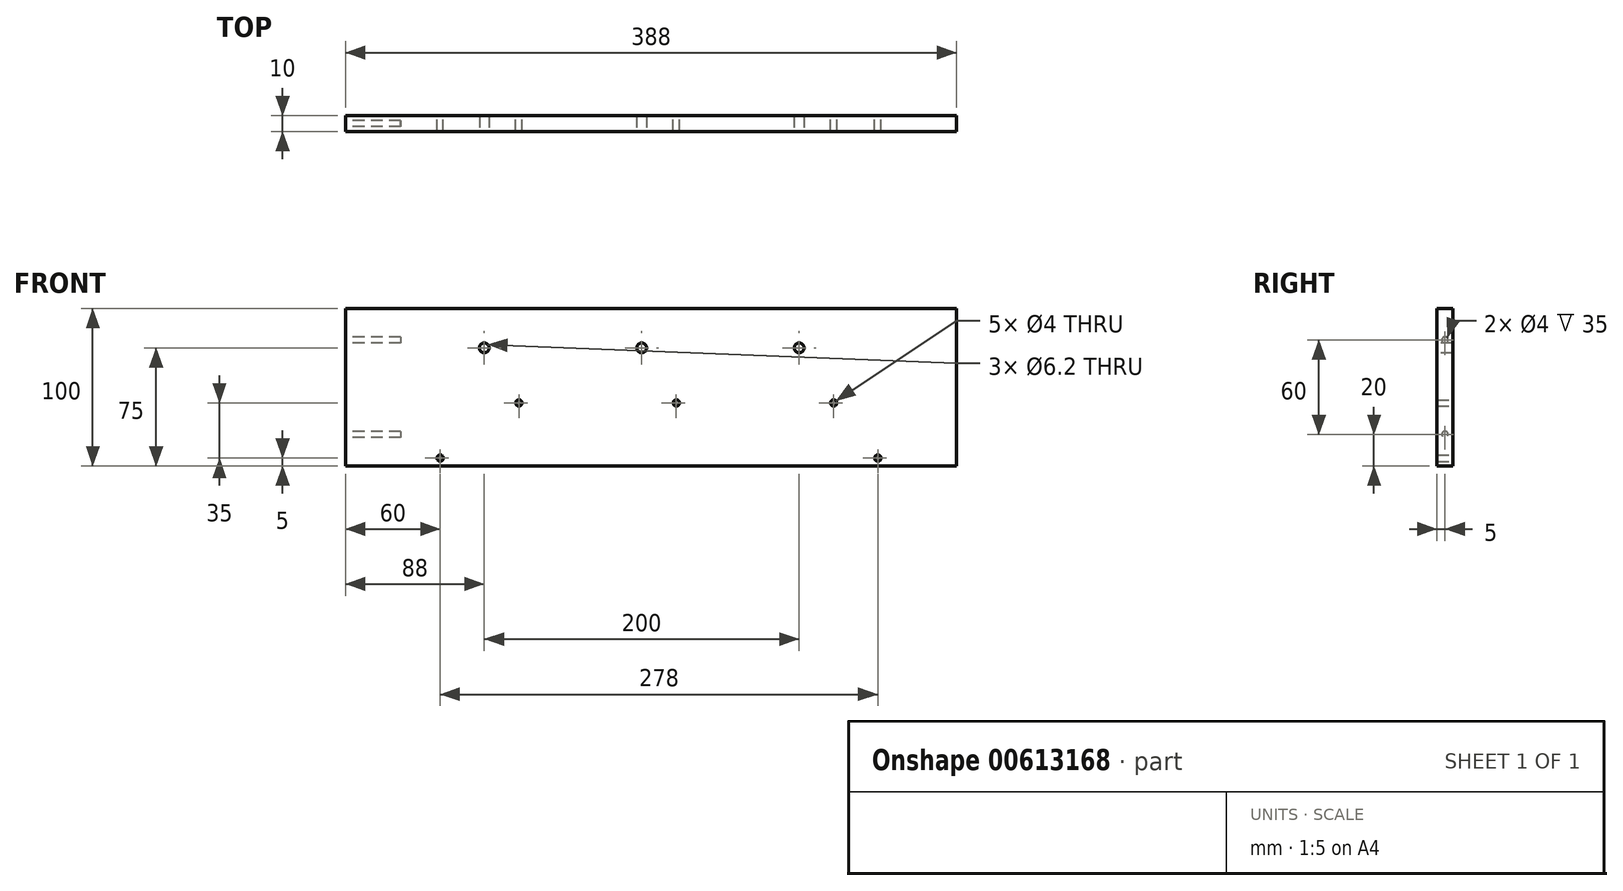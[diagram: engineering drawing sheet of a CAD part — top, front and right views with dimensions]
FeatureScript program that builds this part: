
annotation { "Feature Type Name" : "Feature", "Feature Type Description" : "" }
export const myFeature = defineFeature(function(context is Context, id is Id, definition is map)
    precondition{}
    {
        {
            var Q0;
            Q0=qCreatedBy(makeId("Front.planeOp"),FACE);
            var sketch = newSketch(context, id + "F0", { "sketchPlane" : qUnion([Q0])});
            skLineSegment(sketch, "E0.bottom", {"start": v(194, 50) * mm, "end": v(-194, 50) * mm});
            skLineSegment(sketch, "E0.top", {"start": v(194, -50) * mm, "end": v(-194, -50) * mm});
            skLineSegment(sketch, "E0.left", {"start": v(194, 50) * mm, "end": v(194, -50) * mm});
            skLineSegment(sketch, "E0.right", {"start": v(-194, 50) * mm, "end": v(-194, -50) * mm});
            skPoint(sketch, "E0.middle", {"position": v(0, 0) * mm});
            skCircle(sketch, "E1", {"center": v(144, -45) * mm, "radius": 2 * mm});
            skCircle(sketch, "E2", {"center": v(-134, -45) * mm, "radius": 2 * mm});
            skPoint(sketch, "E3", {"position": v(0, -45) * mm});
            skCircle(sketch, "E4", {"center": v(116, -10) * mm, "radius": 2 * mm});
            skCircle(sketch, "E5", {"center": v(16, -10) * mm, "radius": 2 * mm});
            skCircle(sketch, "E6", {"center": v(-84, -10) * mm, "radius": 2 * mm});
            skLineSegment(sketch, "E7", {"start": v(-84, -10) * mm, "end": v(16, -10) * mm, "construction": true});
            skLineSegment(sketch, "E8", {"start": v(116, -10) * mm, "end": v(16, -10) * mm, "construction": true});
            skSolve(sketch);
        }
        {
            var Q0;
            Q0=qSketchRegion(id+"F0",true);
            extrude(context, id + "F1", {"entities" : qUnion([Q0]), "depth" : 10 * mm, "offsetDistance" : 25 * mm});
        }
        {
            var Q0;
            Q0=makeQuery(id+"F1.opExtrude","CAP_FACE",FACE,{"disambiguationData":[OSD([sQuery(id+"F0.wireOp",EDGE,"E0.bottom"),sQuery(id+"F0.wireOp",EDGE,"E0.top"),sQuery(id+"F0.wireOp",EDGE,"E0.left"),sQuery(id+"F0.wireOp",EDGE,"E0.right"),sQuery(id+"F0.wireOp",EDGE,"E1"),sQuery(id+"F0.wireOp",EDGE,"E2"),sQuery(id+"F0.wireOp",EDGE,"E4"),sQuery(id+"F0.wireOp",EDGE,"E5"),sQuery(id+"F0.wireOp",EDGE,"E6")])],"isStart":false});
            var sketch = newSketch(context, id + "F2", { "sketchPlane" : qUnion([Q0])});
            skCircle(sketch, "E9", {"center": v(-6, 25) * mm, "radius": 3.1 * mm});
            skCircle(sketch, "E10", {"center": v(94, 25) * mm, "radius": 3.1 * mm});
            skCircle(sketch, "E11", {"center": v(-106, 25) * mm, "radius": 3.1 * mm});
            skSolve(sketch);
        }
        {
            var Q0;
            Q0=qSketchRegion(id+"F2",true);
            extrude(context, id + "F3", {"entities" : qUnion([Q0]), "operationType" : NewBodyOperationType.REMOVE, "oppositeDirection" : true, "depth" : 25 * mm, "offsetDistance" : 25 * mm});
        }
        {
            var Q0;
            Q0=makeQuery(id+"F1.opExtrude","SWEPT_FACE",FACE,{"disambiguationData":[OSD([sQuery(id+"F0.wireOp",EDGE,"E0.right")])]});
            var sketch = newSketch(context, id + "F4", { "sketchPlane" : qUnion([Q0])});
            skCircle(sketch, "E12", {"center": v(5, -30) * mm, "radius": 2 * mm});
            skCircle(sketch, "E13", {"center": v(5, 30) * mm, "radius": 2 * mm});
            skPoint(sketch, "E13.centerSnap0", {"position": v(5, 50) * mm});
            skSolve(sketch);
        }
        {
            var Q0;
            Q0=qSketchRegion(id+"F4",true);
            extrude(context, id + "F5", {"entities" : qUnion([Q0]), "operationType" : NewBodyOperationType.REMOVE, "oppositeDirection" : true, "depth" : 35 * mm, "offsetDistance" : 25 * mm});
        }
    });
